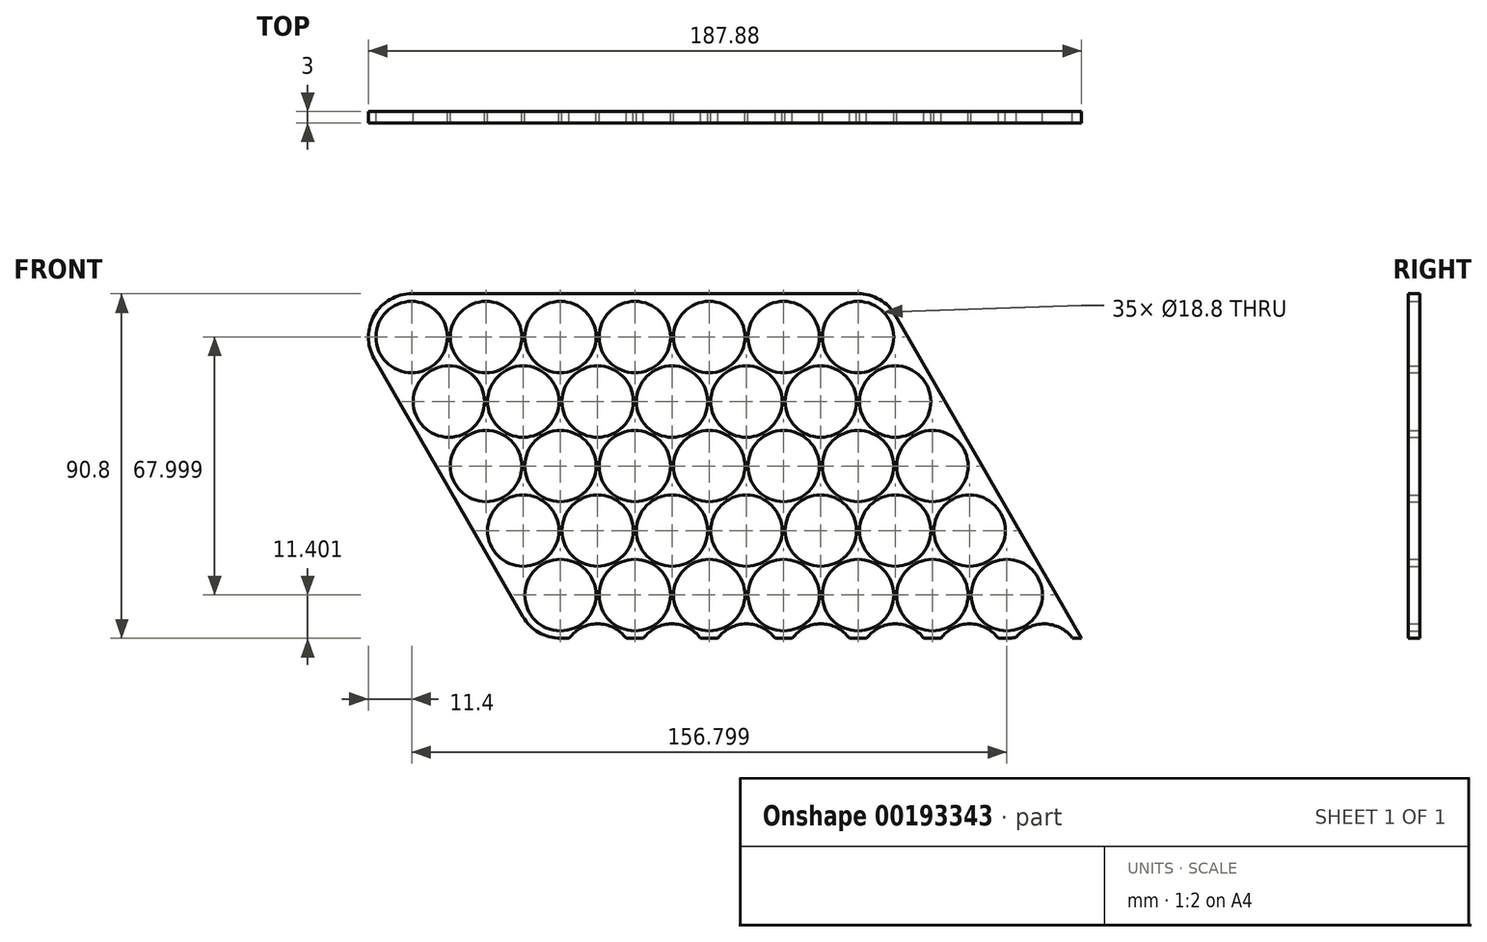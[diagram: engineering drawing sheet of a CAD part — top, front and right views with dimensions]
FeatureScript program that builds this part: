
annotation { "Feature Type Name" : "Feature", "Feature Type Description" : "" }
export const myFeature = defineFeature(function(context is Context, id is Id, definition is map)
    precondition{}
    {
        {
            var Q0;
            Q0=qCreatedBy(makeId("Front.planeOp"),FACE);
            var sketch = newSketch(context, id + "F0", { "sketchPlane" : qUnion([Q0])});
            skCircle(sketch, "E0", {"center": v(0, 0) * mm, "radius": 9.4 * mm});
            skCircle(sketch, "E1.1.0.0", {"center": v(19.6, 0) * mm, "radius": 9.4 * mm});
            skCircle(sketch, "E1.2.0.0", {"center": v(39.2, 0) * mm, "radius": 9.4 * mm});
            skCircle(sketch, "E1.3.0.0", {"center": v(58.8, 0) * mm, "radius": 9.4 * mm});
            skLineSegment(sketch, "E1.direction1", {"start": v(0, 0) * mm, "end": v(19.6, 0) * mm, "construction": true});
            skLineSegment(sketch, "E2", {"start": v(0, -17) * mm, "end": v(73.2, -17) * mm, "construction": true});
            skLineSegment(sketch, "E3", {"start": v(9.8, 0) * mm, "end": v(9.8, -17) * mm, "construction": true});
            skCircle(sketch, "E4", {"center": v(9.8, -17) * mm, "radius": 9.4 * mm});
            skCircle(sketch, "E5.1.0.0", {"center": v(29.4, -17) * mm, "radius": 9.4 * mm});
            skCircle(sketch, "E5.2.0.0", {"center": v(49, -17) * mm, "radius": 9.4 * mm});
            skCircle(sketch, "E5.3.0.0", {"center": v(68.6, -17) * mm, "radius": 9.4 * mm});
            skLineSegment(sketch, "E5.direction1", {"start": v(9.8, -17) * mm, "end": v(29.4, -17) * mm, "construction": true});
            skLineSegment(sketch, "E6", {"start": v(-8.14, -4.7) * mm, "end": v(1.66, -21.7) * mm});
            skLineSegment(sketch, "E7", {"start": v(0, 9.4) * mm, "end": v(58.8, 9.4) * mm});
            skLineSegment(sketch, "E8", {"start": v(9.8, -17) * mm, "end": v(9.8, -26.4) * mm, "construction": true});
            skLineSegment(sketch, "E9", {"start": v(68.6, -17) * mm, "end": v(68.6, -26.4) * mm, "construction": true});
            skArc(sketch, "E10", {"start": v(58.8, 9.4) * mm, "mid": v(63.5, 8.14) * mm, "end": v(66.94, 4.7) * mm});
            skArc(sketch, "E11", {"start": v(76.74, -12.3) * mm, "mid": v(76.74, -21.7) * mm, "end": v(68.6, -26.4) * mm});
            skArc(sketch, "E12", {"start": v(9.8, -26.4) * mm, "mid": v(5.1, -25.14) * mm, "end": v(1.66, -21.7) * mm});
            skArc(sketch, "E13", {"start": v(-8.14, -4.7) * mm, "mid": v(-8.14, 4.7) * mm, "end": v(0, 9.4) * mm});
            skArc(sketch, "E14.0", {"start": v(0, 11.4) * mm, "mid": v(-9.87, 5.7) * mm, "end": v(-9.88, -5.7) * mm});
            skLineSegment(sketch, "E15.0", {"start": v(0, 11.4) * mm, "end": v(58.8, 11.4) * mm});
            skLineSegment(sketch, "E16.0", {"start": v(-9.88, -5.7) * mm, "end": v(-0.08, -22.7) * mm});
            skArc(sketch, "E17.trimOffspring", {"start": v(9.8, -5.82) * mm, "mid": v(9.87, -5.71) * mm, "end": v(9.93, -5.6) * mm});
            skArc(sketch, "E18.trimOffspring", {"start": v(9.93, -5.6) * mm, "mid": v(9.86, -5.6) * mm, "end": v(9.8, -5.6) * mm});
            skCircle(sketch, "E19.0.4.0", {"center": v(78.4, 0) * mm, "radius": 9.4 * mm});
            skCircle(sketch, "E19.0.5.0", {"center": v(98, 0) * mm, "radius": 9.4 * mm});
            skCircle(sketch, "E20.0.4.0", {"center": v(88.2, -17) * mm, "radius": 9.4 * mm});
            skCircle(sketch, "E20.0.5.0", {"center": v(107.8, -17) * mm, "radius": 9.4 * mm});
            skLineSegment(sketch, "E21", {"start": v(58.8, 11.4) * mm, "end": v(98, 11.4) * mm});
            skLineSegment(sketch, "E22", {"start": v(0, 0) * mm, "end": v(9.8, -17) * mm, "construction": true});
            skCircle(sketch, "E23.1.0.0", {"center": v(19.6, -34) * mm, "radius": 9.4 * mm});
            skCircle(sketch, "E23.2.0.0", {"center": v(29.4, -51) * mm, "radius": 9.4 * mm});
            skLineSegment(sketch, "E23.direction1", {"start": v(9.8, -17) * mm, "end": v(19.6, -34) * mm, "construction": true});
            skCircle(sketch, "E24.1.0.0", {"center": v(39.2, -34) * mm, "radius": 9.4 * mm});
            skCircle(sketch, "E24.1.0.1", {"center": v(49, -51) * mm, "radius": 9.4 * mm});
            skCircle(sketch, "E24.2.0.0", {"center": v(58.8, -34) * mm, "radius": 9.4 * mm});
            skCircle(sketch, "E24.2.0.1", {"center": v(68.6, -51) * mm, "radius": 9.4 * mm});
            skCircle(sketch, "E24.3.0.0", {"center": v(78.4, -34) * mm, "radius": 9.4 * mm});
            skCircle(sketch, "E24.3.0.1", {"center": v(88.2, -51) * mm, "radius": 9.4 * mm});
            skCircle(sketch, "E24.4.0.0", {"center": v(98, -34) * mm, "radius": 9.4 * mm});
            skCircle(sketch, "E24.4.0.1", {"center": v(107.8, -51) * mm, "radius": 9.4 * mm});
            skCircle(sketch, "E24.5.0.0", {"center": v(117.6, -34) * mm, "radius": 9.4 * mm});
            skCircle(sketch, "E24.5.0.1", {"center": v(127.4, -51) * mm, "radius": 9.4 * mm});
            skLineSegment(sketch, "E24.direction1", {"start": v(19.6, -34) * mm, "end": v(39.2, -34) * mm, "construction": true});
            skLineSegment(sketch, "E25", {"start": v(-0.08, -22.7) * mm, "end": v(19.52, -56.7) * mm});
            skArc(sketch, "E26.0", {"start": v(29.27, -62.4) * mm, "mid": v(29.33, -62.4) * mm, "end": v(29.4, -62.4) * mm});
            skCircle(sketch, "E27.0.6.0", {"center": v(117.6, 0) * mm, "radius": 9.4 * mm});
            skCircle(sketch, "E28.0.6.0", {"center": v(127.4, -17) * mm, "radius": 9.4 * mm});
            skCircle(sketch, "E29.0.6.0", {"center": v(137.2, -34) * mm, "radius": 9.4 * mm});
            skCircle(sketch, "E29.2.6.0", {"center": v(147, -51) * mm, "radius": 9.4 * mm});
            skLineSegment(sketch, "E30", {"start": v(98, 11.4) * mm, "end": v(117.6, 11.4) * mm});
            skCircle(sketch, "E31.0.3.0", {"center": v(39.2, -68) * mm, "radius": 9.4 * mm});
            skCircle(sketch, "E32.1.0.0", {"center": v(58.8, -68) * mm, "radius": 9.4 * mm});
            skCircle(sketch, "E32.2.0.0", {"center": v(78.4, -68) * mm, "radius": 9.4 * mm});
            skCircle(sketch, "E32.3.0.0", {"center": v(98, -68) * mm, "radius": 9.4 * mm});
            skCircle(sketch, "E32.4.0.0", {"center": v(117.6, -68) * mm, "radius": 9.4 * mm});
            skCircle(sketch, "E32.5.0.0", {"center": v(137.2, -68) * mm, "radius": 9.4 * mm});
            skCircle(sketch, "E32.6.0.0", {"center": v(156.8, -68) * mm, "radius": 9.4 * mm});
            skLineSegment(sketch, "E32.direction1", {"start": v(39.2, -68) * mm, "end": v(58.8, -68) * mm, "construction": true});
            skArc(sketch, "E33.0", {"start": v(29.32, -73.7) * mm, "mid": v(33.5, -77.87) * mm, "end": v(39.2, -79.4) * mm});
            skLineSegment(sketch, "E34", {"start": v(19.52, -56.7) * mm, "end": v(29.32, -73.7) * mm});
            skLineSegment(sketch, "E35", {"start": v(39.2, -79.4) * mm, "end": v(41.45, -79.4) * mm});
            skArc(sketch, "E36", {"start": v(127.48, 5.7) * mm, "mid": v(123.3, 9.87) * mm, "end": v(117.6, 11.4) * mm});
            skArc(sketch, "E37", {"start": v(156.8, -79.4) * mm, "mid": v(158.03, -79.33) * mm, "end": v(159.26, -79.13) * mm});
            skLineSegment(sketch, "E38", {"start": v(127.48, 5.7) * mm, "end": v(166.68, -62.3) * mm});
            skArc(sketch, "E39.0.4.0", {"start": v(56.55, -79.4) * mm, "mid": v(49, -75.6) * mm, "end": v(41.45, -79.4) * mm});
            skArc(sketch, "E40.1.0.0", {"start": v(76.15, -79.4) * mm, "mid": v(68.6, -75.6) * mm, "end": v(61.05, -79.4) * mm});
            skArc(sketch, "E40.2.0.0", {"start": v(95.75, -79.4) * mm, "mid": v(88.2, -75.6) * mm, "end": v(80.65, -79.4) * mm});
            skArc(sketch, "E40.3.0.0", {"start": v(115.35, -79.4) * mm, "mid": v(107.8, -75.6) * mm, "end": v(100.25, -79.4) * mm});
            skArc(sketch, "E40.4.0.0", {"start": v(134.95, -79.4) * mm, "mid": v(127.4, -75.6) * mm, "end": v(119.85, -79.4) * mm});
            skArc(sketch, "E40.5.0.0", {"start": v(154.55, -79.4) * mm, "mid": v(147, -75.6) * mm, "end": v(139.45, -79.4) * mm});
            skArc(sketch, "E40.6.0.0", {"start": v(165.2, -75.7) * mm, "mid": v(161.9, -76.85) * mm, "end": v(159.26, -79.13) * mm});
            skLineSegment(sketch, "E40.direction1", {"start": v(49, -85) * mm, "end": v(68.6, -85) * mm, "construction": true});
            skLineSegment(sketch, "E41.trimOffspring", {"start": v(154.55, -79.4) * mm, "end": v(156.8, -79.4) * mm});
            skLineSegment(sketch, "E42.trimOffspring", {"start": v(134.95, -79.4) * mm, "end": v(139.45, -79.4) * mm});
            skLineSegment(sketch, "E43.trimOffspring", {"start": v(115.35, -79.4) * mm, "end": v(119.85, -79.4) * mm});
            skLineSegment(sketch, "E44.trimOffspring", {"start": v(95.75, -79.4) * mm, "end": v(100.25, -79.4) * mm});
            skLineSegment(sketch, "E45.trimOffspring", {"start": v(76.15, -79.4) * mm, "end": v(80.65, -79.4) * mm});
            skLineSegment(sketch, "E46.trimOffspring", {"start": v(56.55, -79.4) * mm, "end": v(61.05, -79.4) * mm});
            skArc(sketch, "E47", {"start": v(174.08, -79.3) * mm, "mid": v(166.7, -75.6) * mm, "end": v(159.26, -79.13) * mm});
            skLineSegment(sketch, "E48", {"start": v(166.68, -62.3) * mm, "end": v(176.48, -79.3) * mm});
            skLineSegment(sketch, "E49", {"start": v(156.8, -68) * mm, "end": v(166.6, -85) * mm, "construction": true});
            skLineSegment(sketch, "E50", {"start": v(166.6, -85) * mm, "end": v(185.3, -117.44) * mm, "construction": true});
            skLineSegment(sketch, "E51", {"start": v(176.48, -79.3) * mm, "end": v(174.08, -79.3) * mm});
            skSolve(sketch);
        }
        {
            var Q0;
            Q0=qSketchRegion(id+"F0",true);
            var Q1;
            {var subQ3=sQuery(id+"F0.wireOp",EDGE,"E1.1.0.0");Q1=makeQuery(id+"F0.imprint","IMPRINT",FACE,{"disambiguationData":[TD([[makeQuery(id+"F0.imprint","IMPRINT",EDGE,{"derivedFrom":subQ3}),-1.0]])]});}
            extrude(context, id + "F1", {"entities" : qUnion([Q0, Q1]), "depth" : 3 * mm});
        }
    });
